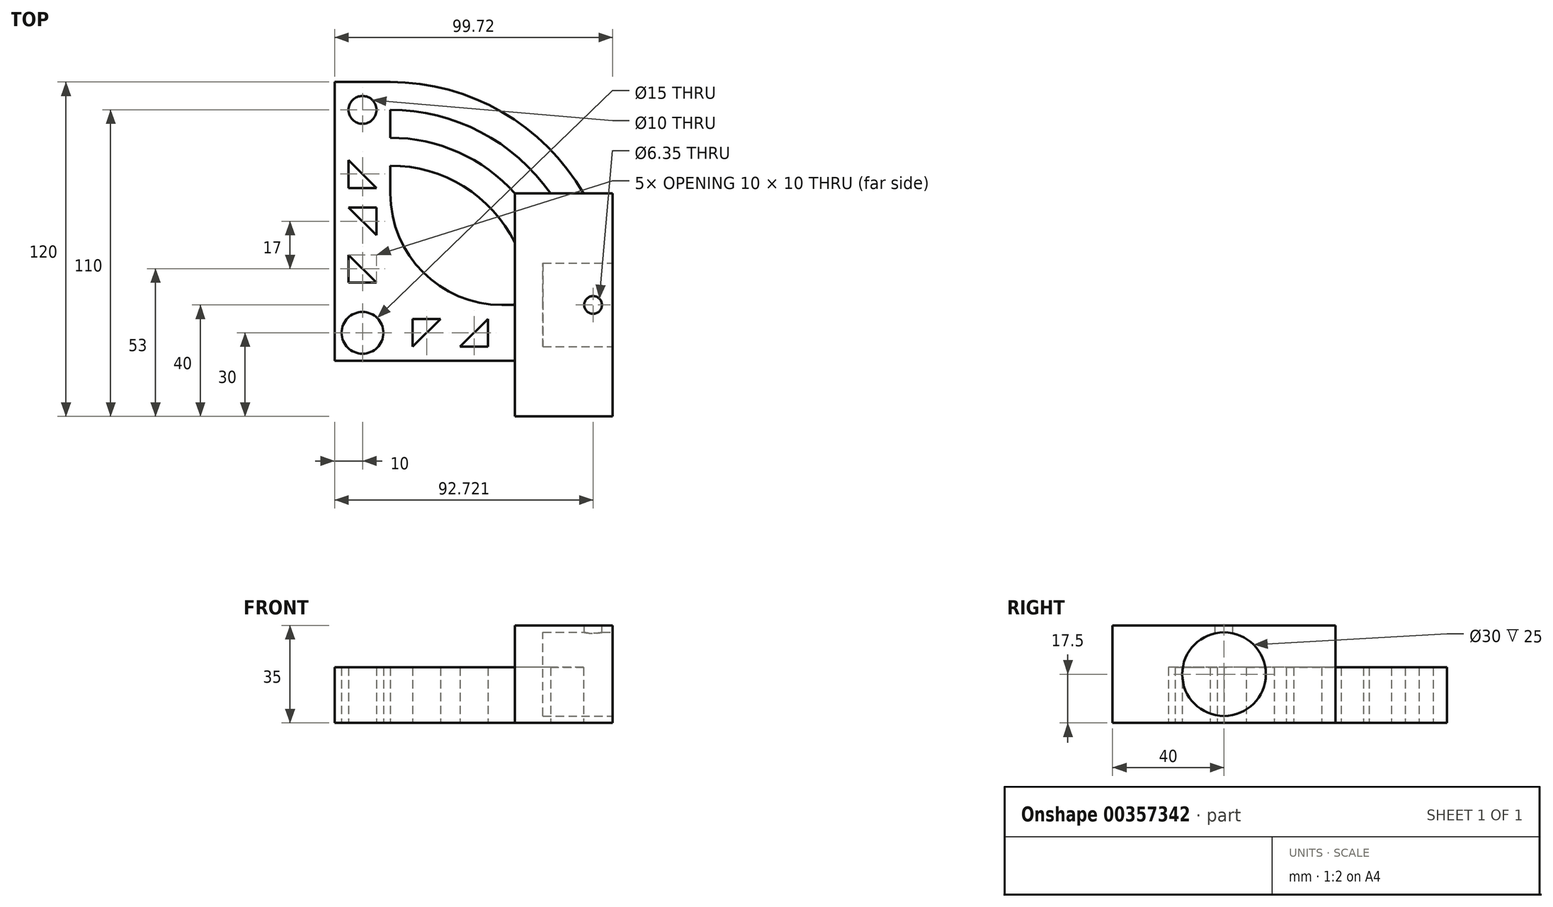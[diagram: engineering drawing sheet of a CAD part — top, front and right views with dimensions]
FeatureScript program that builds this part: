
annotation { "Feature Type Name" : "Feature", "Feature Type Description" : "" }
export const myFeature = defineFeature(function(context is Context, id is Id, definition is map)
    precondition{}
    {
        {
            var Q0;
            Q0=qCreatedBy(makeId("Top.planeOp"),FACE);
            var sketch = newSketch(context, id + "F0", { "sketchPlane" : qUnion([Q0])});
            skLineSegment(sketch, "E0.bottom", {"start": v(0, 80) * mm, "end": v(-20, 80) * mm});
            skLineSegment(sketch, "E0.top", {"start": v(0, -20) * mm, "end": v(-20, -20) * mm});
            skLineSegment(sketch, "E0.left", {"start": v(0, 80) * mm, "end": v(0, 40) * mm});
            skLineSegment(sketch, "E0.right", {"start": v(-20, 80) * mm, "end": v(-20, -20) * mm});
            skLineSegment(sketch, "E1.bottom", {"start": v(40, 0) * mm, "end": v(43.72, 0) * mm});
            skLineSegment(sketch, "E1.top", {"start": v(0, -20) * mm, "end": v(43.72, -20) * mm});
            skLineSegment(sketch, "E1.left", {"start": v(0, 0) * mm, "end": v(0, -20) * mm});
            skLineSegment(sketch, "E1.right", {"start": v(80, 0) * mm, "end": v(80, -20) * mm});
            skCircle(sketch, "E2", {"center": v(-10, -10) * mm, "radius": 7.5 * mm});
            skLineSegment(sketch, "E3", {"start": v(-5, 25) * mm, "end": v(-15, 35) * mm});
            skLineSegment(sketch, "E4", {"start": v(-15, 35) * mm, "end": v(-5, 35) * mm});
            skLineSegment(sketch, "E5", {"start": v(-5, 35) * mm, "end": v(-5, 25) * mm});
            skLineSegment(sketch, "E6", {"start": v(-15, 18) * mm, "end": v(-5, 8) * mm});
            skLineSegment(sketch, "E7", {"start": v(-5, 8) * mm, "end": v(-15, 8) * mm});
            skLineSegment(sketch, "E8", {"start": v(-15, 8) * mm, "end": v(-15, 18) * mm});
            skCircle(sketch, "E9", {"center": v(-10, 70) * mm, "radius": 5 * mm});
            skLineSegment(sketch, "E10", {"start": v(-15, 52) * mm, "end": v(-5, 42) * mm});
            skLineSegment(sketch, "E11", {"start": v(-5, 42) * mm, "end": v(-15, 42) * mm});
            skLineSegment(sketch, "E12", {"start": v(-15, 42) * mm, "end": v(-15, 52) * mm});
            skLineSegment(sketch, "E13", {"start": v(25, -15) * mm, "end": v(35, -5) * mm});
            skLineSegment(sketch, "E14", {"start": v(35, -5) * mm, "end": v(35, -15) * mm});
            skLineSegment(sketch, "E15", {"start": v(35, -15) * mm, "end": v(25, -15) * mm});
            skLineSegment(sketch, "E16", {"start": v(18, -5) * mm, "end": v(8, -15) * mm});
            skLineSegment(sketch, "E17", {"start": v(8, -15) * mm, "end": v(8, -5) * mm});
            skLineSegment(sketch, "E18", {"start": v(8, -5) * mm, "end": v(18, -5) * mm});
            skCircle(sketch, "E19", {"center": v(0, 0) * mm, "radius": 80 * mm});
            skCircle(sketch, "E20", {"center": v(0, 0) * mm, "radius": 70 * mm});
            skCircle(sketch, "E21", {"center": v(0, 0) * mm, "radius": 60 * mm});
            skCircle(sketch, "E22", {"center": v(0, 0) * mm, "radius": 50 * mm});
            skPoint(sketch, "E23", {"position": v(0, 50) * mm});
            skPoint(sketch, "E24", {"position": v(50, 0) * mm});
            skLineSegment(sketch, "E25.bottom", {"start": v(79.72, -40) * mm, "end": v(44.72, -40) * mm});
            skLineSegment(sketch, "E25.top", {"start": v(79.72, 40) * mm, "end": v(44.72, 40) * mm});
            skLineSegment(sketch, "E25.left", {"start": v(79.72, -40) * mm, "end": v(79.72, 40) * mm});
            skLineSegment(sketch, "E25.right", {"start": v(44.72, 1) * mm, "end": v(44.72, 40) * mm});
            skPoint(sketch, "E26", {"position": v(44.72, 0) * mm});
            skPoint(sketch, "E27.newPointA", {"position": v(80, 0) * mm});
            skPoint(sketch, "E27.newPointB", {"position": v(44.72, -40) * mm});
            skArc(sketch, "E27.filletArc", {"start": v(43.72, 0) * mm, "mid": v(44.43, 0.3) * mm, "end": v(44.72, 1) * mm});
            skLineSegment(sketch, "E28", {"start": v(44.72, -21) * mm, "end": v(44.72, -40) * mm});
            skPoint(sketch, "E29.newPointA", {"position": v(80, -20) * mm});
            skLineSegment(sketch, "E30", {"start": v(44.72, 1) * mm, "end": v(44.72, -21) * mm});
            skArc(sketch, "E31.filletArc", {"start": v(0, 40) * mm, "mid": v(11.72, 11.72) * mm, "end": v(40, 0) * mm});
            skLineSegment(sketch, "E32", {"start": v(43.72, -20) * mm, "end": v(44.72, -20) * mm});
            skSolve(sketch);
        }
        {
            var Q0;
            {var subQ11=sQuery(id+"F0.wireOp",EDGE,"E0.top");Q0=makeQuery(id+"F0.imprint","IMPRINT",FACE,{"disambiguationData":[TD([[makeQuery(id+"F0.imprint","IMPRINT",EDGE,{"derivedFrom":subQ11}),-1.0]])]});}
            var Q1;
            {var subQ5=sQuery(id+"F0.wireOp",EDGE,"E21");var subQ6=sQuery(id+"F0.wireOp",EDGE,"E0.left");var subQ7=makeQuery(id+"F0.imprint","INTERSECT",VERTEX,{"derivedFrom":[subQ6,subQ5]});Q1=makeQuery(id+"F0.imprint","IMPRINT",FACE,{"disambiguationData":[TD([[makeQuery(id+"F0.imprint","IMPRINT",EDGE,{"disambiguationData":[TD([[subQ7,-1.0]])],"derivedFrom":subQ6}),-1.0]])]});}
            var Q2;
            {var subQ0=sQuery(id+"F0.wireOp",EDGE,"E20");var subQ1=sQuery(id+"F0.wireOp",EDGE,"E0.left");var subQ2=makeQuery(id+"F0.imprint","INTERSECT",VERTEX,{"derivedFrom":[subQ1,subQ0]});Q2=makeQuery(id+"F0.imprint","IMPRINT",FACE,{"disambiguationData":[TD([[makeQuery(id+"F0.imprint","IMPRINT",EDGE,{"disambiguationData":[TD([[subQ2,-1.0]])],"derivedFrom":subQ1}),-1.0]])]});}
            var Q3;
            {var subQ0=sQuery(id+"F0.wireOp",EDGE,"E19");var subQ3=sQuery(id+"F0.wireOp",EDGE,"E0.right");var subQ4=makeQuery(id+"F0.imprint","INTERSECT",VERTEX,{"derivedFrom":[subQ3,subQ0]});Q3=makeQuery(id+"F0.imprint","IMPRINT",FACE,{"disambiguationData":[TD([[makeQuery(id+"F0.imprint","IMPRINT",EDGE,{"disambiguationData":[TD([[subQ4,-1.0]])],"derivedFrom":subQ3}),1.0]])]});}
            var Q4;
            {var subQ0=sQuery(id+"F0.wireOp",EDGE,"E0.bottom");Q4=makeQuery(id+"F0.imprint","IMPRINT",FACE,{"disambiguationData":[TD([[makeQuery(id+"F0.imprint","IMPRINT",EDGE,{"derivedFrom":subQ0}),1.0]])]});}
            var Q5;
            {var subQ3=sQuery(id+"F0.wireOp",EDGE,"E22");var subQ5=sQuery(id+"F0.wireOp",EDGE,"E25.right");var subQ8=makeQuery(id+"F0.imprint","INTERSECT",VERTEX,{"derivedFrom":[subQ3,subQ5]});Q5=makeQuery(id+"F0.imprint","IMPRINT",FACE,{"disambiguationData":[TD([[makeQuery(id+"F0.imprint","IMPRINT",EDGE,{"disambiguationData":[TD([[subQ8,1.0]])],"derivedFrom":subQ3}),1.0]])]});}
            var Q6;
            {var subQ3=sQuery(id+"F0.wireOp",EDGE,"E25.right");var subQ5=sQuery(id+"F0.wireOp",EDGE,"E22");var subQ7=makeQuery(id+"F0.imprint","INTERSECT",VERTEX,{"derivedFrom":[subQ5,subQ3]});Q6=makeQuery(id+"F0.imprint","IMPRINT",FACE,{"disambiguationData":[TD([[makeQuery(id+"F0.imprint","IMPRINT",EDGE,{"disambiguationData":[TD([[subQ7,1.0]])],"derivedFrom":subQ5}),-1.0]])]});}
            var Q7;
            {var subQ0=sQuery(id+"F0.wireOp",EDGE,"E25.top");var subQ1=sQuery(id+"F0.wireOp",EDGE,"E20");var subQ2=makeQuery(id+"F0.imprint","INTERSECT",VERTEX,{"derivedFrom":[subQ1,subQ0]});Q7=makeQuery(id+"F0.imprint","IMPRINT",FACE,{"disambiguationData":[TD([[makeQuery(id+"F0.imprint","IMPRINT",EDGE,{"disambiguationData":[TD([[subQ2,1.0]])],"derivedFrom":subQ1}),1.0]])]});}
            var Q8;
            {var subQ1=sQuery(id+"F0.wireOp",EDGE,"E19");var subQ7=sQuery(id+"F0.wireOp",EDGE,"E25.left");var subQ8=makeQuery(id+"F0.imprint","INTERSECT",VERTEX,{"disambiguationData":[OD(0.0)],"derivedFrom":[subQ1,subQ7]});Q8=makeQuery(id+"F0.imprint","IMPRINT",FACE,{"disambiguationData":[TD([[makeQuery(id+"F0.imprint","IMPRINT",EDGE,{"disambiguationData":[TD([[subQ8,-1.0]])],"derivedFrom":subQ1}),1.0]])]});}
            var Q9;
            {var subQ1=sQuery(id+"F0.wireOp",EDGE,"E0.left");var subQ3=sQuery(id+"F0.wireOp",EDGE,"E20");var subQ4=makeQuery(id+"F0.imprint","INTERSECT",VERTEX,{"derivedFrom":[subQ1,subQ3]});Q9=makeQuery(id+"F0.imprint","IMPRINT",FACE,{"disambiguationData":[TD([[makeQuery(id+"F0.imprint","IMPRINT",EDGE,{"disambiguationData":[TD([[subQ4,1.0]])],"derivedFrom":subQ3}),-1.0]])]});}
            var Q10;
            {var subQ0=sQuery(id+"F0.wireOp",EDGE,"E21");var subQ1=sQuery(id+"F0.wireOp",EDGE,"E0.left");var subQ2=makeQuery(id+"F0.imprint","INTERSECT",VERTEX,{"derivedFrom":[subQ1,subQ0]});Q10=makeQuery(id+"F0.imprint","IMPRINT",FACE,{"disambiguationData":[TD([[makeQuery(id+"F0.imprint","IMPRINT",EDGE,{"disambiguationData":[TD([[subQ2,-1.0]])],"derivedFrom":subQ1}),1.0]])]});}
            var Q11;
            {var subQ0=sQuery(id+"F0.wireOp",EDGE,"E25.left");var subQ1=sQuery(id+"F0.wireOp",EDGE,"E19");var subQ2=makeQuery(id+"F0.imprint","INTERSECT",VERTEX,{"disambiguationData":[OD(0.0)],"derivedFrom":[subQ1,subQ0]});Q11=makeQuery(id+"F0.imprint","IMPRINT",FACE,{"disambiguationData":[TD([[makeQuery(id+"F0.imprint","IMPRINT",EDGE,{"disambiguationData":[TD([[subQ2,-1.0]])],"derivedFrom":subQ1}),-1.0]])]});}
            var Q12;
            {var subQ0=sQuery(id+"F0.wireOp",EDGE,"E25.bottom");var subQ1=sQuery(id+"F0.wireOp",EDGE,"E19");var subQ2=makeQuery(id+"F0.imprint","INTERSECT",VERTEX,{"derivedFrom":[subQ1,subQ0]});Q12=makeQuery(id+"F0.imprint","IMPRINT",FACE,{"disambiguationData":[TD([[makeQuery(id+"F0.imprint","IMPRINT",EDGE,{"disambiguationData":[TD([[subQ2,-1.0]])],"derivedFrom":subQ1}),-1.0]])]});}
            extrude(context, id + "F1", {"entities" : qUnion([Q0, Q1, Q2, Q3, Q4, Q5, Q6, Q7, Q8, Q9, Q10, Q11, Q12]), "depth" : 20 * mm});
        }
        {
            var Q0;
            {var subQ3=sQuery(id+"F0.wireOp",EDGE,"E22");var subQ5=sQuery(id+"F0.wireOp",EDGE,"E25.right");var subQ8=makeQuery(id+"F0.imprint","INTERSECT",VERTEX,{"derivedFrom":[subQ3,subQ5]});Q0=makeQuery(id+"F0.imprint","IMPRINT",FACE,{"disambiguationData":[TD([[makeQuery(id+"F0.imprint","IMPRINT",EDGE,{"disambiguationData":[TD([[subQ8,1.0]])],"derivedFrom":subQ3}),1.0]])]});}
            var Q1;
            {var subQ3=sQuery(id+"F0.wireOp",EDGE,"E25.right");var subQ5=sQuery(id+"F0.wireOp",EDGE,"E22");var subQ7=makeQuery(id+"F0.imprint","INTERSECT",VERTEX,{"derivedFrom":[subQ5,subQ3]});Q1=makeQuery(id+"F0.imprint","IMPRINT",FACE,{"disambiguationData":[TD([[makeQuery(id+"F0.imprint","IMPRINT",EDGE,{"disambiguationData":[TD([[subQ7,1.0]])],"derivedFrom":subQ5}),-1.0]])]});}
            var Q2;
            {var subQ0=sQuery(id+"F0.wireOp",EDGE,"E25.top");var subQ1=sQuery(id+"F0.wireOp",EDGE,"E20");var subQ2=makeQuery(id+"F0.imprint","INTERSECT",VERTEX,{"derivedFrom":[subQ1,subQ0]});Q2=makeQuery(id+"F0.imprint","IMPRINT",FACE,{"disambiguationData":[TD([[makeQuery(id+"F0.imprint","IMPRINT",EDGE,{"disambiguationData":[TD([[subQ2,1.0]])],"derivedFrom":subQ1}),1.0]])]});}
            var Q3;
            {var subQ1=sQuery(id+"F0.wireOp",EDGE,"E19");var subQ7=sQuery(id+"F0.wireOp",EDGE,"E25.left");var subQ8=makeQuery(id+"F0.imprint","INTERSECT",VERTEX,{"disambiguationData":[OD(0.0)],"derivedFrom":[subQ1,subQ7]});Q3=makeQuery(id+"F0.imprint","IMPRINT",FACE,{"disambiguationData":[TD([[makeQuery(id+"F0.imprint","IMPRINT",EDGE,{"disambiguationData":[TD([[subQ8,-1.0]])],"derivedFrom":subQ1}),1.0]])]});}
            var Q4;
            {var subQ0=sQuery(id+"F0.wireOp",EDGE,"E25.bottom");var subQ1=sQuery(id+"F0.wireOp",EDGE,"E19");var subQ2=makeQuery(id+"F0.imprint","INTERSECT",VERTEX,{"derivedFrom":[subQ1,subQ0]});Q4=makeQuery(id+"F0.imprint","IMPRINT",FACE,{"disambiguationData":[TD([[makeQuery(id+"F0.imprint","IMPRINT",EDGE,{"disambiguationData":[TD([[subQ2,-1.0]])],"derivedFrom":subQ1}),-1.0]])]});}
            var Q5;
            {var subQ0=sQuery(id+"F0.wireOp",EDGE,"E25.left");var subQ1=sQuery(id+"F0.wireOp",EDGE,"E19");var subQ2=makeQuery(id+"F0.imprint","INTERSECT",VERTEX,{"disambiguationData":[OD(0.0)],"derivedFrom":[subQ1,subQ0]});Q5=makeQuery(id+"F0.imprint","IMPRINT",FACE,{"disambiguationData":[TD([[makeQuery(id+"F0.imprint","IMPRINT",EDGE,{"disambiguationData":[TD([[subQ2,-1.0]])],"derivedFrom":subQ1}),-1.0]])]});}
            extrude(context, id + "F2", {"entities" : qUnion([Q0, Q1, Q2, Q3, Q4, Q5]), "operationType" : NewBodyOperationType.ADD, "depth" : 35 * mm});
        }
        {
            var Q0;
            {var subQ0=sQuery(id+"F0.wireOp",EDGE,"E25.left");Q0=makeQuery(id+"F2.boolean.opBoolean","MERGE",FACE,{"derivedFrom":[makeQuery(id+"F1.opExtrude","SWEPT_FACE",FACE,{"disambiguationData":[OSD([subQ0])]}),makeQuery(id+"F2.opExtrude","SWEPT_FACE",FACE,{"disambiguationData":[OSD([subQ0])]})]});}
            var sketch = newSketch(context, id + "F3", { "sketchPlane" : qUnion([Q0])});
            skCircle(sketch, "E33", {"center": v(0, 17.5) * mm, "radius": 15 * mm});
            skSolve(sketch);
        }
        {
            var Q0;
            Q0 = qSketchRegion(id + "F3", true);
            extrude(context, id + "F4", {"entities" : qUnion([Q0]), "operationType" : NewBodyOperationType.REMOVE, "oppositeDirection" : true, "depth" : 25 * mm});
        }
        {
            var Q0;
            Q0=makeQuery(id+"F2.opExtrude","CAP_FACE",FACE,{"disambiguationData":[OSD([sQuery(id+"F0.wireOp",EDGE,"E25.bottom"),sQuery(id+"F0.wireOp",EDGE,"E25.top"),sQuery(id+"F0.wireOp",EDGE,"E25.left"),sQuery(id+"F0.wireOp",EDGE,"E25.right"),sQuery(id+"F0.wireOp",EDGE,"E28"),sQuery(id+"F0.wireOp",EDGE,"E30")])],"isStart":false});
            var sketch = newSketch(context, id + "F5", { "sketchPlane" : qUnion([Q0])});
            skCircle(sketch, "E34", {"center": v(72.72, 0) * mm, "radius": 3.18 * mm});
            skPoint(sketch, "E34.centerSnap0", {"position": v(44.72, 0) * mm});
            skSolve(sketch);
        }
        {
            var Q0;
            Q0 = qSketchRegion(id + "F5", true);
            extrude(context, id + "F6", {"entities" : qUnion([Q0]), "operationType" : NewBodyOperationType.REMOVE, "oppositeDirection" : true, "depth" : 31.5 * mm});
        }
    });
